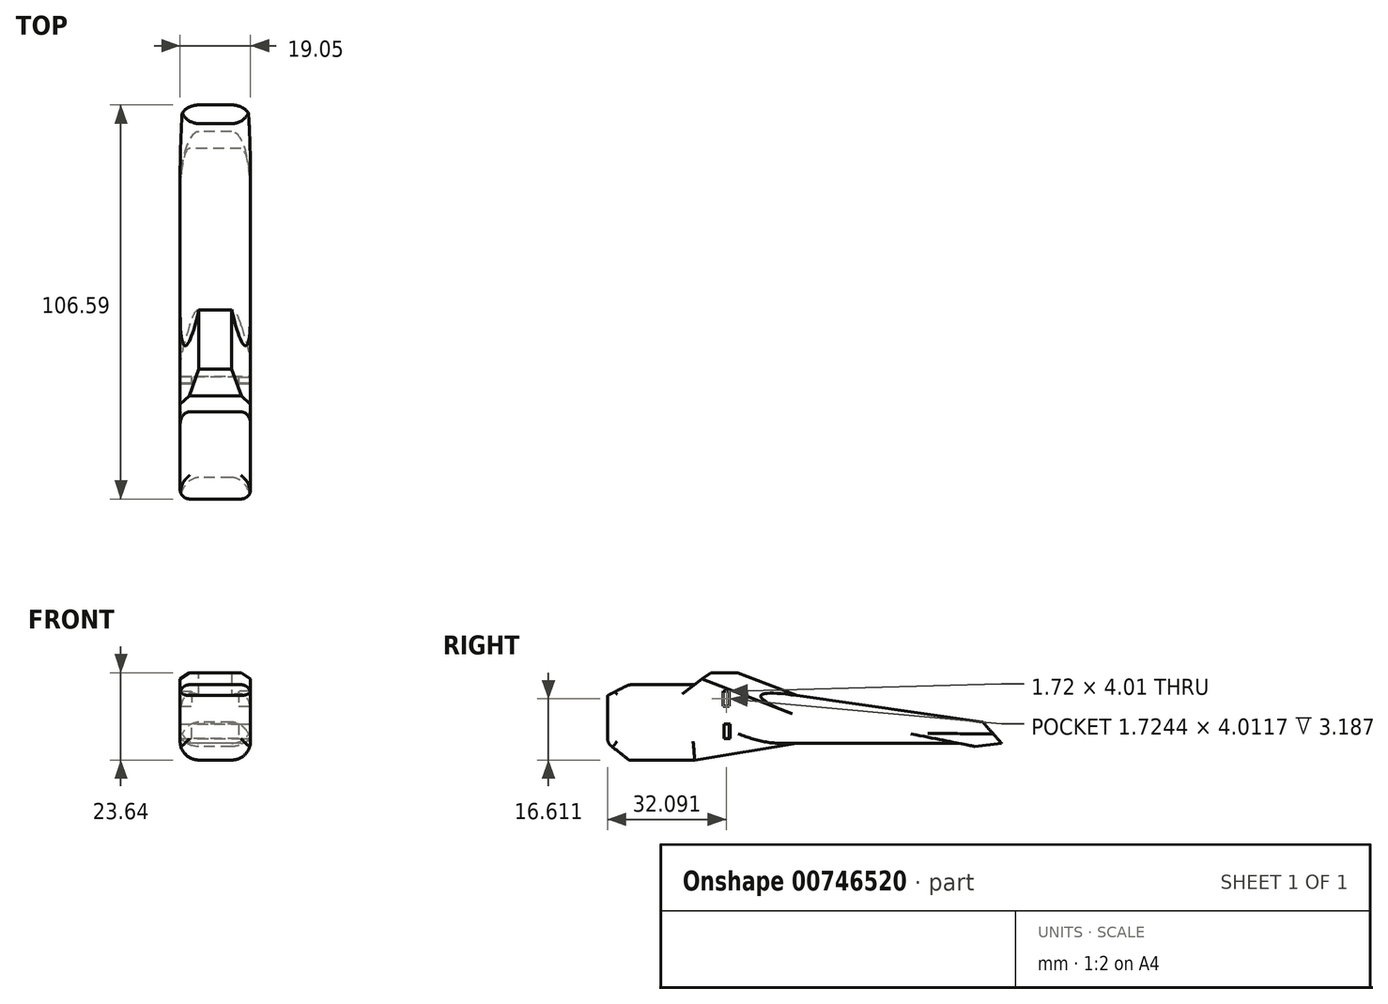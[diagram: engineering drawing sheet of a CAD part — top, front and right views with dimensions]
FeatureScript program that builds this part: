
annotation { "Feature Type Name" : "Feature", "Feature Type Description" : "" }
export const myFeature = defineFeature(function(context is Context, id is Id, definition is map)
    precondition{}
    {
        {
            var Q0;
            Q0=qCreatedBy(makeId("Right.planeOp"),FACE);
            var sketch = newSketch(context, id + "F0", { "sketchPlane" : qUnion([Q0])});
            skLineSegment(sketch, "E0", {"start": v(55.43, 0) * mm, "end": v(50.35, 5.66) * mm});
            skLineSegment(sketch, "E1", {"start": v(50.35, 5.66) * mm, "end": v(0, 12.91) * mm});
            skLineSegment(sketch, "E2", {"start": v(0, 12.91) * mm, "end": v(-16, 19.08) * mm});
            skLineSegment(sketch, "E3", {"start": v(-16, 19.08) * mm, "end": v(-23.25, 19.08) * mm});
            skLineSegment(sketch, "E4", {"start": v(-23.25, 19.08) * mm, "end": v(-27.6, 15.82) * mm});
            skLineSegment(sketch, "E5", {"start": v(-27.6, 15.82) * mm, "end": v(-45.36, 15.82) * mm});
            skLineSegment(sketch, "E6", {"start": v(-45.36, 15.82) * mm, "end": v(-51.16, 12.91) * mm});
            skLineSegment(sketch, "E7", {"start": v(-51.16, 12.91) * mm, "end": v(-51.16, 0) * mm});
            skLineSegment(sketch, "E8", {"start": v(-51.16, 0) * mm, "end": v(-45.36, -4.56) * mm});
            skLineSegment(sketch, "E9", {"start": v(-45.36, -4.56) * mm, "end": v(-27.6, -4.56) * mm});
            skLineSegment(sketch, "E10", {"start": v(-27.6, -4.56) * mm, "end": v(0, 0) * mm});
            skLineSegment(sketch, "E11", {"start": v(0, 0) * mm, "end": v(43.7, 0) * mm});
            skLineSegment(sketch, "E12", {"start": v(43.7, 0) * mm, "end": v(48.2, -0.89) * mm});
            skLineSegment(sketch, "E13", {"start": v(48.2, -0.89) * mm, "end": v(55.43, 0) * mm});
            skSolve(sketch);
        }
        {
            var Q0;
            Q0=qSketchRegion(id+"F0",true);
            extrude(context, id + "F1", {"entities" : qUnion([Q0]), "depth" : 19.05 * mm, "offsetDistance" : 25.4 * mm});
        }
        {
            var Q0;
            Q0=makeQuery(id+"F1.opExtrude","CAP_EDGE",EDGE,{"disambiguationData":[OSD([sQuery(id+"F0.wireOp",EDGE,"E2")])],"isStart":true});
            var Q1;
            Q1=makeQuery(id+"F1.opExtrude","CAP_EDGE",EDGE,{"disambiguationData":[OSD([sQuery(id+"F0.wireOp",EDGE,"E2")])],"isStart":false});
            chamfer(context, id + "F2", {"entities" : qUnion([Q0, Q1]), "width" : 5.08 * mm, "tangentPropagation" : true});
        }
        {
            var Q0;
            Q0=makeQuery(id+"F1.opExtrude","CAP_EDGE",EDGE,{"disambiguationData":[OSD([sQuery(id+"F0.wireOp",EDGE,"E1")])],"isStart":true});
            var Q1;
            Q1=makeQuery(id+"F1.opExtrude","CAP_EDGE",EDGE,{"disambiguationData":[OSD([sQuery(id+"F0.wireOp",EDGE,"E1")])],"isStart":false});
            fillet(context, id + "F3", {"entities" : qUnion([Q0, Q1]), "radius" : 5.08 * mm, "tangentPropagation" : true, "allowEdgeOverflow" : false});
        }
        {
            var Q0;
            Q0=makeQuery(id+"F1.opExtrude","CAP_EDGE",EDGE,{"disambiguationData":[OSD([sQuery(id+"F0.wireOp",EDGE,"E11")])],"isStart":true});
            var Q1;
            Q1=makeQuery(id+"F1.opExtrude","CAP_EDGE",EDGE,{"disambiguationData":[OSD([sQuery(id+"F0.wireOp",EDGE,"E11")])],"isStart":false});
            fillet(context, id + "F4", {"entities" : qUnion([Q0, Q1]), "radius" : 2.54 * mm, "tangentPropagation" : true, "allowEdgeOverflow" : false});
        }
        {
            var Q0;
            Q0=makeQuery(id+"F1.opExtrude","CAP_EDGE",EDGE,{"disambiguationData":[OSD([sQuery(id+"F0.wireOp",EDGE,"E5")])],"isStart":true});
            var Q1;
            Q1=makeQuery(id+"F1.opExtrude","CAP_EDGE",EDGE,{"disambiguationData":[OSD([sQuery(id+"F0.wireOp",EDGE,"E5")])],"isStart":false});
            var Q2;
            Q2=makeQuery(id+"F1.opExtrude","SWEPT_EDGE",EDGE,{"disambiguationData":[OSD([sQuery(id+"F0.wireOp",EDGE,"E5"),sQuery(id+"F0.wireOp",EDGE,"E6")])]});
            var Q3;
            Q3=makeQuery(id+"F1.opExtrude","CAP_EDGE",EDGE,{"disambiguationData":[OSD([sQuery(id+"F0.wireOp",EDGE,"E7")])],"isStart":true});
            var Q4;
            Q4=makeQuery(id+"F1.opExtrude","CAP_EDGE",EDGE,{"disambiguationData":[OSD([sQuery(id+"F0.wireOp",EDGE,"E7")])],"isStart":false});
            var Q5;
            Q5=makeQuery(id+"F1.opExtrude","SWEPT_EDGE",EDGE,{"disambiguationData":[OSD([sQuery(id+"F0.wireOp",EDGE,"E7"),sQuery(id+"F0.wireOp",EDGE,"E8")])]});
            fillet(context, id + "F5", {"entities" : qUnion([Q0, Q1, Q2, Q3, Q4, Q5]), "radius" : 2.54 * mm, "tangentPropagation" : true, "allowEdgeOverflow" : false});
        }
        {
            var Q0;
            Q0=makeQuery(id+"F1.opExtrude","CAP_EDGE",EDGE,{"disambiguationData":[OSD([sQuery(id+"F0.wireOp",EDGE,"E13")])],"isStart":true});
            var Q1;
            Q1=makeQuery(id+"F1.opExtrude","CAP_EDGE",EDGE,{"disambiguationData":[OSD([sQuery(id+"F0.wireOp",EDGE,"E13")])],"isStart":false});
            var Q2;
            Q2=makeQuery(id+"F1.opExtrude","CAP_EDGE",EDGE,{"disambiguationData":[OSD([sQuery(id+"F0.wireOp",EDGE,"E10")])],"isStart":true});
            var Q3;
            Q3=makeQuery(id+"F1.opExtrude","CAP_EDGE",EDGE,{"disambiguationData":[OSD([sQuery(id+"F0.wireOp",EDGE,"E10")])],"isStart":false});
            var Q4;
            Q4=makeQuery(id+"F1.opExtrude","CAP_EDGE",EDGE,{"disambiguationData":[OSD([sQuery(id+"F0.wireOp",EDGE,"E9")])],"isStart":false});
            var Q5;
            Q5=makeQuery(id+"F1.opExtrude","CAP_EDGE",EDGE,{"disambiguationData":[OSD([sQuery(id+"F0.wireOp",EDGE,"E9")])],"isStart":true});
            fillet(context, id + "F6", {"entities" : qUnion([Q0, Q1, Q2, Q3, Q4, Q5]), "radius" : 5.08 * mm, "tangentPropagation" : true, "allowEdgeOverflow" : false});
        }
        {
            var Q0;
            Q0=makeQuery(id+"F1.opExtrude","CAP_FACE",FACE,{"disambiguationData":[OSD([sQuery(id+"F0.wireOp",EDGE,"E0"),sQuery(id+"F0.wireOp",EDGE,"E1"),sQuery(id+"F0.wireOp",EDGE,"E2"),sQuery(id+"F0.wireOp",EDGE,"E3"),sQuery(id+"F0.wireOp",EDGE,"E4"),sQuery(id+"F0.wireOp",EDGE,"E5"),sQuery(id+"F0.wireOp",EDGE,"E6"),sQuery(id+"F0.wireOp",EDGE,"E7"),sQuery(id+"F0.wireOp",EDGE,"E8"),sQuery(id+"F0.wireOp",EDGE,"E9"),sQuery(id+"F0.wireOp",EDGE,"E10"),sQuery(id+"F0.wireOp",EDGE,"E11"),sQuery(id+"F0.wireOp",EDGE,"E12"),sQuery(id+"F0.wireOp",EDGE,"E13")])],"isStart":false});
            var sketch = newSketch(context, id + "F7", { "sketchPlane" : qUnion([Q0])});
            skLineSegment(sketch, "E14", {"start": v(-45.7, 9.96) * mm, "end": v(-15.18, 9.96) * mm});
            skLineSegment(sketch, "E15", {"start": v(-45.67, 5.2) * mm, "end": v(-15.34, 5.2) * mm});
            skSolve(sketch);
        }
        {
            var Q0;
            {var subQ7=sQuery(id+"F0.wireOp",EDGE,"E4");Q0=makeQuery(id+"F7.imprint","IMPRINT",FACE,{"disambiguationData":[TD([[makeQuery(id+"F7.imprint","IMPRINT",EDGE,{"derivedFrom":makeQuery(id+"F1.opExtrude","CAP_EDGE",EDGE,{"disambiguationData":[OSD([subQ7])],"isStart":false})}),1.0]])]});}
            var sketch = newSketch(context, id + "F8", { "sketchPlane" : qUnion([Q0])});
            skLineSegment(sketch, "E16.bottom", {"start": v(-19.93, 10.04) * mm, "end": v(-18.2, 10.04) * mm});
            skLineSegment(sketch, "E16.top", {"start": v(-19.93, 14.06) * mm, "end": v(-18.2, 14.06) * mm});
            skLineSegment(sketch, "E16.left", {"start": v(-19.93, 10.04) * mm, "end": v(-19.93, 14.06) * mm});
            skLineSegment(sketch, "E16.right", {"start": v(-18.2, 10.04) * mm, "end": v(-18.2, 14.06) * mm});
            skLineSegment(sketch, "E17.bottom", {"start": v(-19.69, 5.22) * mm, "end": v(-17.96, 5.22) * mm});
            skLineSegment(sketch, "E17.top", {"start": v(-19.69, 1.21) * mm, "end": v(-17.96, 1.21) * mm});
            skLineSegment(sketch, "E17.left", {"start": v(-19.69, 5.22) * mm, "end": v(-19.69, 1.21) * mm});
            skLineSegment(sketch, "E17.right", {"start": v(-17.96, 5.22) * mm, "end": v(-17.96, 1.21) * mm});
            skSolve(sketch);
        }
        {
            var Q0;
            Q0 = qSketchRegion(id + "F8", true);
            extrude(context, id + "F9", {"entities" : qUnion([Q0]), "operationType" : NewBodyOperationType.REMOVE, "oppositeDirection" : true, "depth" : 29.7 * mm, "offsetDistance" : 25.4 * mm});
        }
        {
            var Q0;
            Q0=makeQuery(id+"F9.boolean.opBoolean","COPY",FACE,{"derivedFrom":makeQuery(id+"F9.opExtrude","SWEPT_FACE",FACE,{"disambiguationData":[OSD([sQuery(id+"F8.wireOp",EDGE,"E16.bottom")])]})});
            var sketch = newSketch(context, id + "F10", { "sketchPlane" : qUnion([Q0])});
            skLineSegment(sketch, "E18", {"start": v(9.53, -18.2) * mm, "end": v(15.86, -18.2) * mm});
            skLineSegment(sketch, "E19", {"start": v(15.86, -18.2) * mm, "end": v(15.86, -19.93) * mm});
            skLineSegment(sketch, "E20", {"start": v(15.86, -19.93) * mm, "end": v(9.53, -19.93) * mm});
            skLineSegment(sketch, "E21", {"start": v(9.53, -19.93) * mm, "end": v(3.17, -19.93) * mm});
            skLineSegment(sketch, "E22", {"start": v(3.17, -19.93) * mm, "end": v(3.17, -18.2) * mm});
            skLineSegment(sketch, "E23", {"start": v(3.17, -18.2) * mm, "end": v(9.53, -18.2) * mm});
            skSolve(sketch);
        }
        {
            var Q0;
            Q0 = qSketchRegion(id + "F10", true);
            extrude(context, id + "F11", {"entities" : qUnion([Q0]), "operationType" : NewBodyOperationType.ADD, "depth" : 4 * mm, "offsetDistance" : 25.4 * mm});
        }
        {
            var Q0;
            Q0 = qSketchRegion(id + "F10", true);
            extrude(context, id + "F12", {"entities" : qUnion([Q0]), "operationType" : NewBodyOperationType.ADD, "oppositeDirection" : true, "depth" : 10.03 * mm, "offsetDistance" : 25.4 * mm});
        }
    });
